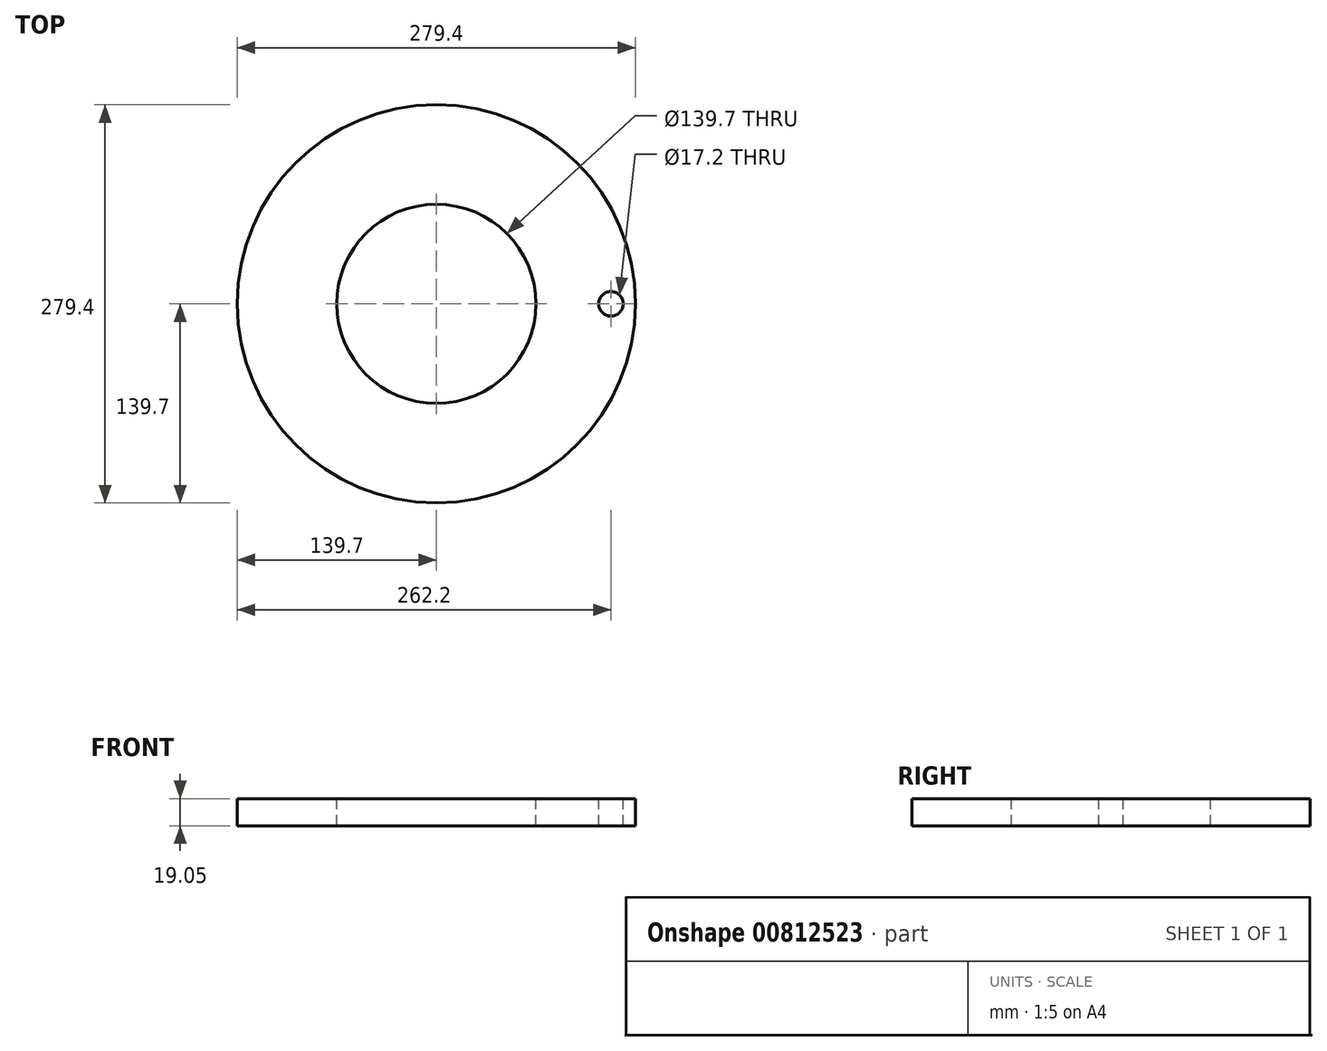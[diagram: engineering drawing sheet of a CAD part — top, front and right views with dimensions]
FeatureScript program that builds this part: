
annotation { "Feature Type Name" : "Feature", "Feature Type Description" : "" }
export const myFeature = defineFeature(function(context is Context, id is Id, definition is map)
    precondition{}
    {
        {
            var Q0;
            Q0=qCreatedBy(makeId("Top.planeOp"),FACE);
            var sketch = newSketch(context, id + "F0", { "sketchPlane" : qUnion([Q0])});
            skCircle(sketch, "E0", {"center": v(0, 0) * mm, "radius": 139.7 * mm});
            skSolve(sketch);
        }
        {
            var Q0;
            Q0=makeQuery(id+"F0.imprint","IMPRINT",FACE,{"disambiguationData":[TD([[makeQuery(id+"F0.imprint","IMPRINT",EDGE,{"derivedFrom":sQuery(id+"F0.wireOp",EDGE,"E0")}),1.0]])]});
            extrude(context, id + "F1", {"entities" : qUnion([Q0]), "depth" : 19.05 * mm, "offsetDistance" : 25.4 * mm});
        }
        {
            var Q0;
            Q0=makeQuery(id+"F1.opExtrude","CAP_FACE",FACE,{"disambiguationData":[OSD([sQuery(id+"F0.wireOp",EDGE,"E0")])],"isStart":false});
            var sketch = newSketch(context, id + "F2", { "sketchPlane" : qUnion([Q0])});
            skCircle(sketch, "E1", {"center": v(0, 0) * mm, "radius": 69.85 * mm});
            skSolve(sketch);
        }
        {
            var Q0;
            Q0=makeQuery(id+"F2.imprint","IMPRINT",FACE,{"disambiguationData":[TD([[makeQuery(id+"F2.imprint","IMPRINT",EDGE,{"derivedFrom":sQuery(id+"F2.wireOp",EDGE,"E1")}),1.0]])]});
            extrude(context, id + "F3", {"entities" : qUnion([Q0]), "operationType" : NewBodyOperationType.REMOVE, "endBound" : BoundingType.THROUGH_ALL, "oppositeDirection" : true, "depth" : 25.4 * mm, "offsetDistance" : 25.4 * mm});
        }
        {
            var Q0;
            Q0=makeQuery(id+"F1.opExtrude","CAP_FACE",FACE,{"disambiguationData":[OSD([sQuery(id+"F0.wireOp",EDGE,"E0")])],"isStart":false});
            var sketch = newSketch(context, id + "F4", { "sketchPlane" : qUnion([Q0])});
            skCircle(sketch, "E2", {"center": v(122.5, 0) * mm, "radius": 8.6 * mm});
            skCircle(sketch, "E3", {"center": v(0, 0) * mm, "radius": 122.5 * mm, "construction": true});
            skSolve(sketch);
        }
        {
            var Q0;
            Q0=makeQuery(id+"F4.imprint","IMPRINT",FACE,{"disambiguationData":[TD([[makeQuery(id+"F4.imprint","IMPRINT",EDGE,{"derivedFrom":sQuery(id+"F4.wireOp",EDGE,"E2")}),1.0]])]});
            extrude(context, id + "F5", {"entities" : qUnion([Q0]), "operationType" : NewBodyOperationType.REMOVE, "endBound" : BoundingType.THROUGH_ALL, "oppositeDirection" : true, "depth" : 25.4 * mm, "offsetDistance" : 25.4 * mm});
        }
    });
